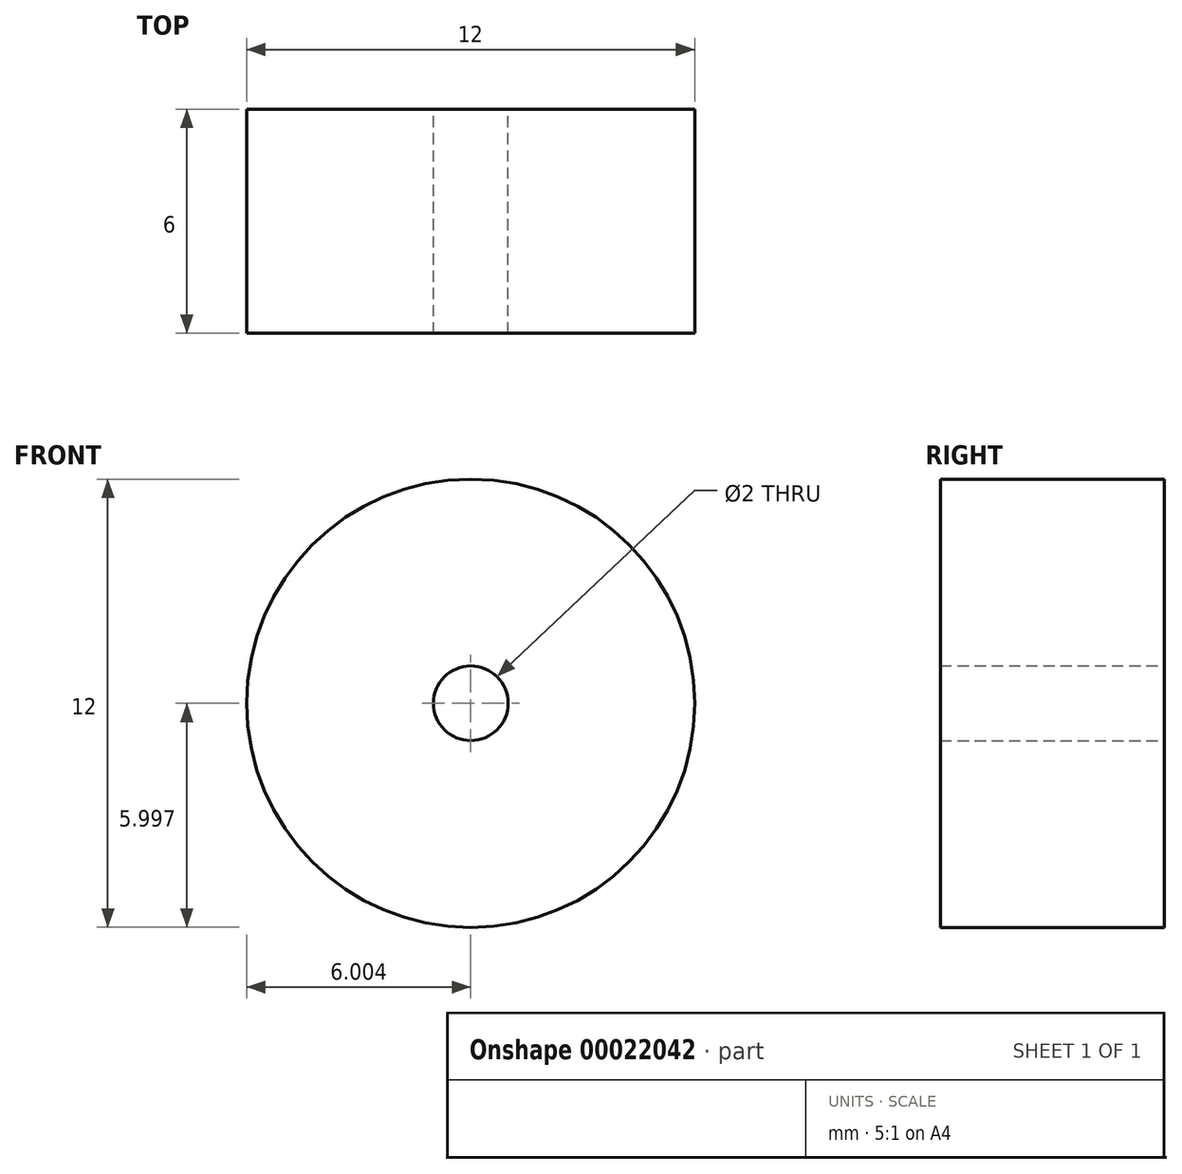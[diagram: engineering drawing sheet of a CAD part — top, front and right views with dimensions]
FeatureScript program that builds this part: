
annotation { "Feature Type Name" : "Feature", "Feature Type Description" : "" }
export const myFeature = defineFeature(function(context is Context, id is Id, definition is map)
    precondition{}
    {
        {
            var Q0;
            Q0=qCreatedBy(makeId("Front.planeOp"),FACE);
            var sketch = newSketch(context, id + "F0", { "sketchPlane" : qUnion([Q0])});
            skCircle(sketch, "E0", {"center": v(-55.79, 9.02) * mm, "radius": 6 * mm});
            skCircle(sketch, "E1", {"center": v(-55.79, 9.02) * mm, "radius": 1 * mm});
            skSolve(sketch);
        }
        {
            var Q0;
            Q0=makeQuery(id+"F0.imprint","IMPRINT",FACE,{"disambiguationData":[TD([[makeQuery(id+"F0.imprint","IMPRINT",EDGE,{"derivedFrom":sQuery(id+"F0.wireOp",EDGE,"E0")}),1.0]])]});
            extrude(context, id + "F1", {"entities" : qUnion([Q0]), "endBound" : BoundingType.SYMMETRIC, "depth" : 6 * mm});
        }
    });
